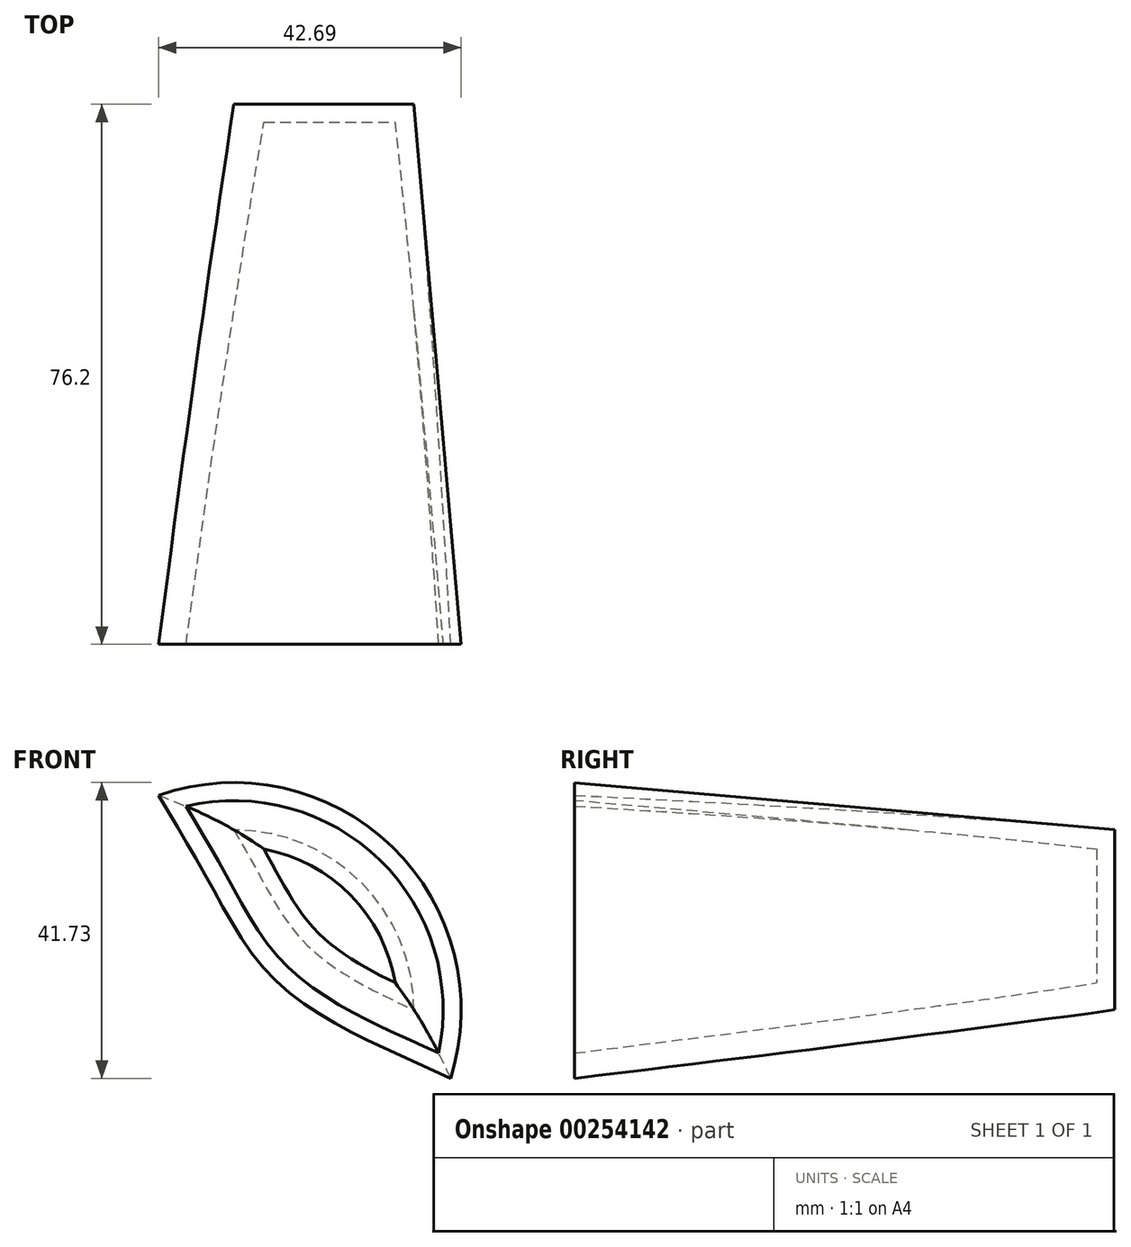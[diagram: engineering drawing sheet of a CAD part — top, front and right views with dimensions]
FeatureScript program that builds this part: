
annotation { "Feature Type Name" : "Feature", "Feature Type Description" : "" }
export const myFeature = defineFeature(function(context is Context, id is Id, definition is map)
    precondition{}
    {
        {
            var Q0;
            Q0=qCreatedBy(makeId("Front.planeOp"),FACE);
            var sketch = newSketch(context, id + "F0", { "sketchPlane" : qUnion([Q0])});
            skPoint(sketch, "E0.middle", {"position": v(0, 0) * mm});
            skPoint(sketch, "E1.visualSharp", {"position": v(-76.2, 50.8) * mm});
            skPoint(sketch, "E2.visualSharp", {"position": v(76.2, 50.8) * mm});
            skArc(sketch, "E2.filletArc", {"start": v(76.2, 25.4) * mm, "mid": v(68.76, 43.36) * mm, "end": v(50.8, 50.8) * mm});
            skPoint(sketch, "E3.visualSharp", {"position": v(76.2, -50.8) * mm});
            skPoint(sketch, "E4.visualSharp", {"position": v(-76.2, -50.8) * mm});
            skArc(sketch, "E4.filletArc", {"start": v(-76.2, -25.4) * mm, "mid": v(-68.76, -43.36) * mm, "end": v(-50.8, -50.8) * mm});
            skFitSpline(sketch, "E5", {"points": [v(5.85, -59.9) * mm, v(-50.8, -50.8) * mm, v(-76.06, -28.06) * mm, v(-105.7, 0) * mm, v(-76.2, 25.4) * mm, v(-50.8, 50.8) * mm, v(-41.31, 71.95) * mm, v(-3.44, 60.6) * mm, v(27.54, 72.64) * mm, v(50.8, 50.8) * mm, v(60.25, 35.46) * mm, v(76.2, 25.4) * mm, v(99.84, 7.57) * mm, v(88.48, -21.34) * mm, v(76.2, -25.4) * mm, v(62.31, -31.33) * mm, v(50.8, -50.8) * mm, v(5.85, -59.9) * mm]});
            skSolve(sketch);
        }
        {
            var Q0;
            Q0=makeQuery(id+"F0.imprint","IMPRINT",FACE,{"disambiguationData":[TD([[makeQuery(id+"F0.imprint","IMPRINT",EDGE,{"derivedFrom":sQuery(id+"F0.wireOp",EDGE,"E2.filletArc")}),1.0]])]});
            extrude(context, id + "F1", {"entities" : qUnion([Q0]), "depth" : 76.2 * mm, "hasDraft" : true, "draftAngle" : 5 * degree});
        }
        {
            var Q0;
            Q0=makeQuery(id+"F1.opExtrude","CAP_FACE",FACE,{"disambiguationData":[OSD([sQuery(id+"F0.wireOp",EDGE,"E2.filletArc"),sQuery(id+"F0.wireOp",EDGE,"E4.filletArc"),sQuery(id+"F0.wireOp",EDGE,"E5"),sQuery(id+"F0.wireOp",EDGE,"E5")])],"isStart":false});
            shell(context, id + "F2", {"entities" : qUnion([Q0]), "thickness" : 2.54 * mm});
        }
    });
